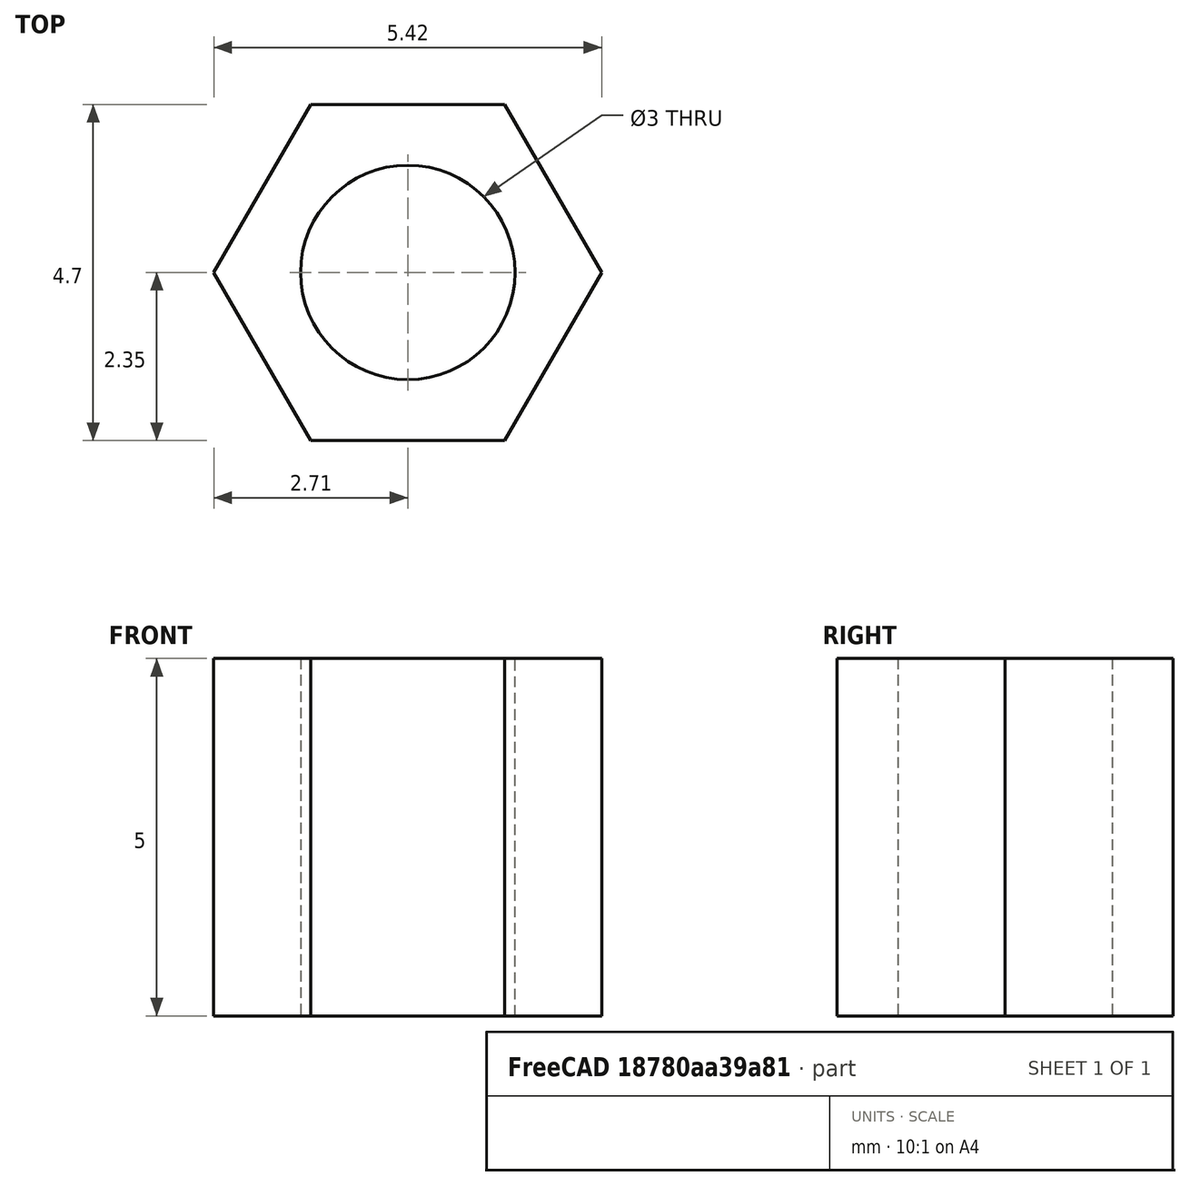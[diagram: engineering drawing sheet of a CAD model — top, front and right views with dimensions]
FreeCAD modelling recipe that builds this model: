
FCSTD DOCUMENT  (FreeCAD 0.18.4R)
Label: coxial_M3_5mm
License: All rights reserved
LicenseURL: http://en.wikipedia.org/wiki/All_rights_reserved
objects: Sketcher::SketchObject×1, PartDesign::Pad×1, PartDesign::Body×1
note: 4 computed .brp shape members not serialized (recipe doc carries the construction recipe); baked Part::Feature solids carry a one-line shape summary decoded from their .brp

FEATURE [Sketcher::SketchObject] Sketch
  MapMode = 5
  Support = -> [XY_Plane]
  sketch-geometry (8):
    g0: Circle CenterX=0 CenterY=0 CenterZ=0 NormalX=0 NormalY=0 NormalZ=1 AngleXU=0 Radius=1.5
    g1: LineSegment StartX=1.35677 StartY=-2.35 StartZ=0 EndX=2.71355 EndY=-4e-16 EndZ=0
    g2: LineSegment StartX=2.71355 StartY=-6e-16 StartZ=0 EndX=1.35677 EndY=2.35 EndZ=0
    g3: LineSegment StartX=1.35677 StartY=2.35 StartZ=0 EndX=-1.35677 EndY=2.35 EndZ=0
    g4: LineSegment StartX=-1.35677 StartY=2.35 StartZ=0 EndX=-2.71355 EndY=1.3e-15 EndZ=0
    g5: LineSegment StartX=-2.71355 StartY=1.3e-15 StartZ=0 EndX=-1.35677 EndY=-2.35 EndZ=0
    g6: LineSegment StartX=-1.35677 StartY=-2.35 StartZ=0 EndX=1.35677 EndY=-2.35 EndZ=0
    g7: Circle [constr] CenterX=0 CenterY=0 CenterZ=0 NormalX=0 NormalY=0 NormalZ=1 AngleXU=0 Radius=2.71355
  constraints (18):
    c: Coincident(g0,g-1)
    c: Radius(g0) = 1.5
    c: Coincident(g1,g2)
    c: Coincident(g2,g3)
    c: Coincident(g3,g4)
    c: Coincident(g4,g5)
    c: Coincident(g5,g6)
    c: Coincident(g6,g1)
    c: Equal(g1, g2-g6) x5
    c: PointOnObject(g1,g7)
    c: PointOnObject(g2,g7)
    c: PointOnObject(g3,g7)
    c: PointOnObject(g4,g7)
    c: PointOnObject(g5,g7)
    c: PointOnObject(g6,g7)
    c: Distance(g2,g4) = 4.7
    c: Coincident(g7,g0)
    c: Horizontal(g3)
FEATURE [PartDesign::Pad] Pad
  Length = 5
  Length2 = 100
  Profile = -> Sketch
  Type = 0
FEATURE [PartDesign::Body] Body
  Group = -> [Sketch,Pad]
  Origin = -> Origin
  Tip = -> Pad
